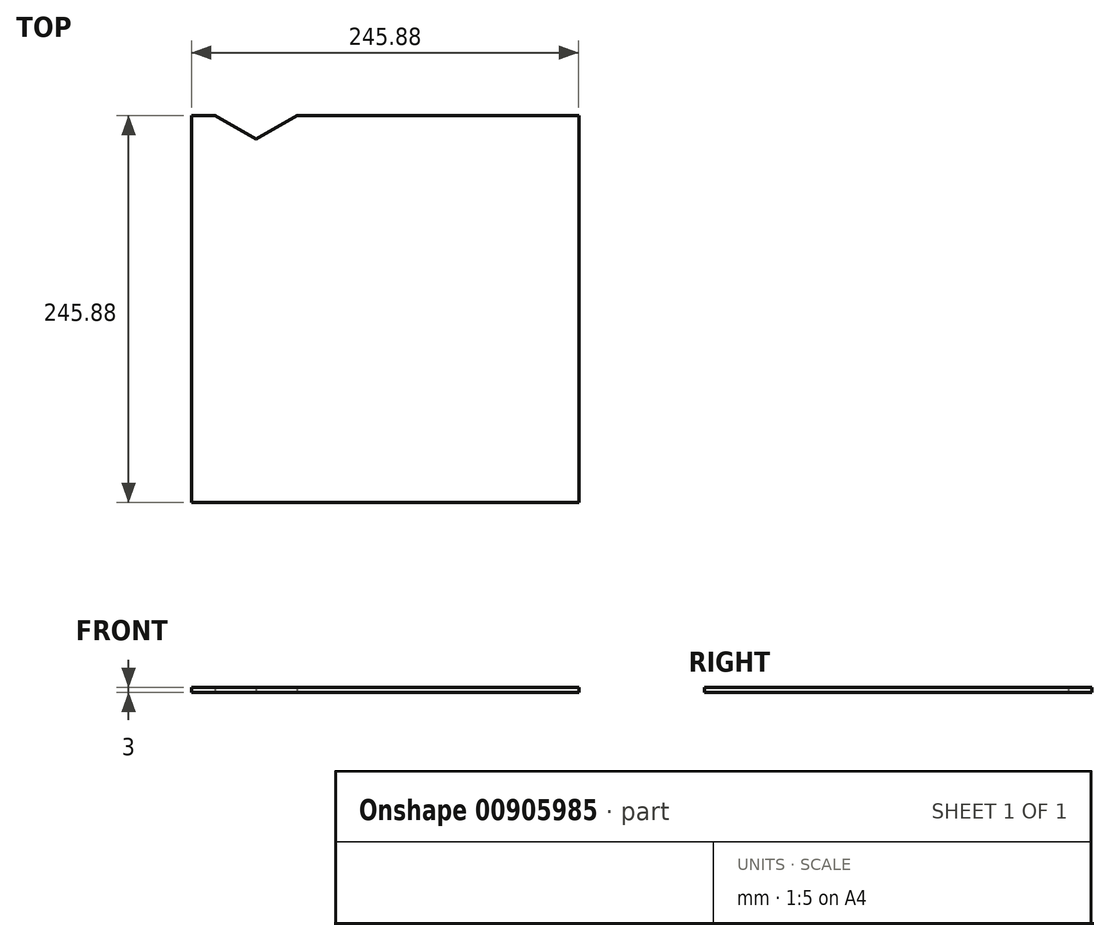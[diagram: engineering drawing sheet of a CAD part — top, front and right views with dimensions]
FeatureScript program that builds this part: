
annotation { "Feature Type Name" : "Feature", "Feature Type Description" : "" }
export const myFeature = defineFeature(function(context is Context, id is Id, definition is map)
    precondition{}
    {
        {
            var Q0;
            Q0=qCreatedBy(makeId("Top.planeOp"),FACE);
            var sketch = newSketch(context, id + "F0", { "sketchPlane" : qUnion([Q0])});
            skLineSegment(sketch, "E0", {"start": v(15, 0) * mm, "end": v(0, -25.98) * mm});
            skLineSegment(sketch, "E1", {"start": v(0, -25.98) * mm, "end": v(-15, 0) * mm});
            skLineSegment(sketch, "E2", {"start": v(-15, 0) * mm, "end": v(0, 25.98) * mm});
            skLineSegment(sketch, "E3", {"start": v(0, 25.98) * mm, "end": v(15, 0) * mm});
            skLineSegment(sketch, "E4", {"start": v(-15, 0) * mm, "end": v(-40.98, 15) * mm});
            skLineSegment(sketch, "E5", {"start": v(-40.98, 15) * mm, "end": v(-25.98, 40.98) * mm});
            skLineSegment(sketch, "E6", {"start": v(-25.98, 40.98) * mm, "end": v(0, 25.98) * mm});
            skLineSegment(sketch, "E7", {"start": v(0, 25.98) * mm, "end": v(25.98, 40.98) * mm});
            skLineSegment(sketch, "E8", {"start": v(25.98, 40.98) * mm, "end": v(40.98, 15) * mm});
            skLineSegment(sketch, "E9", {"start": v(40.98, 15) * mm, "end": v(15, 0) * mm});
            skLineSegment(sketch, "E10", {"start": v(15, 0) * mm, "end": v(40.98, -15) * mm});
            skLineSegment(sketch, "E11", {"start": v(40.98, -15) * mm, "end": v(25.98, -40.98) * mm});
            skLineSegment(sketch, "E12", {"start": v(25.98, -40.98) * mm, "end": v(0, -25.98) * mm});
            skLineSegment(sketch, "E13", {"start": v(-15, 0) * mm, "end": v(-40.98, -15) * mm});
            skLineSegment(sketch, "E14", {"start": v(-40.98, -15) * mm, "end": v(-25.98, -40.98) * mm});
            skLineSegment(sketch, "E15", {"start": v(-25.98, -40.98) * mm, "end": v(0, -25.98) * mm});
            skLineSegment(sketch, "E16", {"start": v(-40.98, 15) * mm, "end": v(-66.96, 0) * mm});
            skLineSegment(sketch, "E17", {"start": v(-66.96, 0) * mm, "end": v(-40.98, -15) * mm});
            skLineSegment(sketch, "E18", {"start": v(40.98, 15) * mm, "end": v(66.96, 0) * mm});
            skLineSegment(sketch, "E19", {"start": v(66.96, 0) * mm, "end": v(40.98, -15) * mm});
            skLineSegment(sketch, "E20", {"start": v(0, 25.98) * mm, "end": v(0, 55.98) * mm});
            skLineSegment(sketch, "E21", {"start": v(-25.98, 40.98) * mm, "end": v(0, 55.98) * mm});
            skLineSegment(sketch, "E22", {"start": v(25.98, 40.98) * mm, "end": v(0, 55.98) * mm});
            skLineSegment(sketch, "E23", {"start": v(0, -25.98) * mm, "end": v(0, -55.98) * mm});
            skLineSegment(sketch, "E24", {"start": v(0, -55.98) * mm, "end": v(-25.98, -40.98) * mm});
            skLineSegment(sketch, "E25", {"start": v(0, -55.98) * mm, "end": v(25.98, -40.98) * mm});
            skLineSegment(sketch, "E26", {"start": v(-40.98, 15) * mm, "end": v(-55.98, 40.98) * mm});
            skLineSegment(sketch, "E27", {"start": v(-55.98, 40.98) * mm, "end": v(-81.96, 25.98) * mm});
            skLineSegment(sketch, "E28", {"start": v(-81.96, 25.98) * mm, "end": v(-66.96, 0) * mm});
            skLineSegment(sketch, "E29", {"start": v(-40.98, -15) * mm, "end": v(-55.98, -40.98) * mm});
            skLineSegment(sketch, "E30", {"start": v(-55.98, -40.98) * mm, "end": v(-81.96, -25.98) * mm});
            skLineSegment(sketch, "E31", {"start": v(-81.96, -25.98) * mm, "end": v(-66.96, 0) * mm});
            skLineSegment(sketch, "E32", {"start": v(-55.98, 40.98) * mm, "end": v(-40.98, 66.96) * mm});
            skLineSegment(sketch, "E33", {"start": v(-40.98, 66.96) * mm, "end": v(-25.98, 40.98) * mm});
            skLineSegment(sketch, "E34", {"start": v(-40.98, 66.96) * mm, "end": v(-15, 81.96) * mm});
            skLineSegment(sketch, "E35", {"start": v(-15, 81.96) * mm, "end": v(0, 55.98) * mm});
            skLineSegment(sketch, "E36", {"start": v(-55.98, 40.98) * mm, "end": v(-81.96, 55.98) * mm});
            skLineSegment(sketch, "E37", {"start": v(-81.96, 55.98) * mm, "end": v(-66.96, 81.96) * mm});
            skLineSegment(sketch, "E38", {"start": v(-66.96, 81.96) * mm, "end": v(-40.98, 66.96) * mm});
            skLineSegment(sketch, "E39", {"start": v(15, 81.96) * mm, "end": v(40.98, 66.96) * mm});
            skLineSegment(sketch, "E40", {"start": v(40.98, 66.96) * mm, "end": v(25.98, 40.98) * mm});
            skLineSegment(sketch, "E41", {"start": v(40.98, 66.96) * mm, "end": v(55.98, 40.98) * mm});
            skLineSegment(sketch, "E42", {"start": v(55.98, 40.98) * mm, "end": v(40.98, 15) * mm});
            skLineSegment(sketch, "E43", {"start": v(-81.96, 55.98) * mm, "end": v(-81.96, 25.98) * mm});
            skLineSegment(sketch, "E44", {"start": v(-81.96, 25.98) * mm, "end": v(-107.94, 40.98) * mm});
            skLineSegment(sketch, "E45", {"start": v(-107.94, 40.98) * mm, "end": v(-81.96, 55.98) * mm});
            skLineSegment(sketch, "E46", {"start": v(55.98, 40.98) * mm, "end": v(81.96, 25.98) * mm});
            skLineSegment(sketch, "E47", {"start": v(81.96, 25.98) * mm, "end": v(66.96, 0) * mm});
            skLineSegment(sketch, "E48", {"start": v(55.98, 40.98) * mm, "end": v(81.96, 55.98) * mm});
            skLineSegment(sketch, "E49", {"start": v(81.96, 55.98) * mm, "end": v(66.96, 81.96) * mm});
            skLineSegment(sketch, "E50", {"start": v(66.96, 81.96) * mm, "end": v(40.98, 66.96) * mm});
            skLineSegment(sketch, "E51", {"start": v(81.96, 55.98) * mm, "end": v(81.96, 25.98) * mm});
            skLineSegment(sketch, "E52", {"start": v(81.96, 25.98) * mm, "end": v(107.94, 40.98) * mm});
            skLineSegment(sketch, "E53", {"start": v(107.94, 40.98) * mm, "end": v(81.96, 55.98) * mm});
            skLineSegment(sketch, "E54", {"start": v(81.96, 55.98) * mm, "end": v(96.96, 81.96) * mm});
            skLineSegment(sketch, "E55", {"start": v(96.96, 81.96) * mm, "end": v(122.94, 66.96) * mm});
            skLineSegment(sketch, "E56", {"start": v(122.94, 66.96) * mm, "end": v(107.94, 40.98) * mm});
            skLineSegment(sketch, "E57", {"start": v(-81.96, 55.98) * mm, "end": v(-96.96, 81.96) * mm});
            skLineSegment(sketch, "E58", {"start": v(-96.96, 81.96) * mm, "end": v(-122.94, 66.96) * mm});
            skLineSegment(sketch, "E59", {"start": v(-122.94, 66.96) * mm, "end": v(-107.94, 40.98) * mm});
            skLineSegment(sketch, "E60", {"start": v(-107.94, 40.98) * mm, "end": v(-122.94, 15) * mm});
            skLineSegment(sketch, "E61", {"start": v(-122.94, 15) * mm, "end": v(-96.96, 0) * mm});
            skLineSegment(sketch, "E62", {"start": v(-96.96, 0) * mm, "end": v(-81.96, 25.98) * mm});
            skLineSegment(sketch, "E63", {"start": v(-96.96, 0) * mm, "end": v(-81.96, -25.98) * mm});
            skLineSegment(sketch, "E64", {"start": v(-81.96, -25.98) * mm, "end": v(-107.94, -40.98) * mm});
            skLineSegment(sketch, "E65", {"start": v(-107.94, -40.98) * mm, "end": v(-122.94, -15) * mm});
            skLineSegment(sketch, "E66", {"start": v(-122.94, -15) * mm, "end": v(-96.96, 0) * mm});
            skLineSegment(sketch, "E67", {"start": v(81.96, 25.98) * mm, "end": v(96.96, 0) * mm});
            skLineSegment(sketch, "E68", {"start": v(96.96, 0) * mm, "end": v(122.94, 15) * mm});
            skLineSegment(sketch, "E69", {"start": v(122.94, 15) * mm, "end": v(107.94, 40.98) * mm});
            skLineSegment(sketch, "E70", {"start": v(66.96, 0) * mm, "end": v(81.96, -25.98) * mm});
            skLineSegment(sketch, "E71", {"start": v(81.96, -25.98) * mm, "end": v(96.96, 0) * mm});
            skLineSegment(sketch, "E72", {"start": v(81.96, -25.98) * mm, "end": v(107.94, -40.98) * mm});
            skLineSegment(sketch, "E73", {"start": v(107.94, -40.98) * mm, "end": v(122.94, -15) * mm});
            skLineSegment(sketch, "E74", {"start": v(122.94, -15) * mm, "end": v(96.96, 0) * mm});
            skLineSegment(sketch, "E75", {"start": v(40.98, 15) * mm, "end": v(40.98, -15) * mm});
            skLineSegment(sketch, "E76", {"start": v(81.96, -25.98) * mm, "end": v(55.98, -40.98) * mm});
            skLineSegment(sketch, "E77", {"start": v(55.98, -40.98) * mm, "end": v(40.98, -15) * mm});
            skLineSegment(sketch, "E78", {"start": v(-40.98, 15) * mm, "end": v(-40.98, -15) * mm});
            skLineSegment(sketch, "E79", {"start": v(-81.96, -25.98) * mm, "end": v(-81.96, -55.98) * mm});
            skLineSegment(sketch, "E80", {"start": v(-81.96, -55.98) * mm, "end": v(-107.94, -40.98) * mm});
            skLineSegment(sketch, "E81", {"start": v(-81.96, -55.98) * mm, "end": v(-55.98, -40.98) * mm});
            skLineSegment(sketch, "E82", {"start": v(-55.98, -40.98) * mm, "end": v(-40.98, -66.96) * mm});
            skLineSegment(sketch, "E83", {"start": v(-40.98, -66.96) * mm, "end": v(-25.98, -40.98) * mm});
            skLineSegment(sketch, "E84", {"start": v(-81.96, -55.98) * mm, "end": v(-66.96, -81.96) * mm});
            skLineSegment(sketch, "E85", {"start": v(-66.96, -81.96) * mm, "end": v(-40.98, -66.96) * mm});
            skLineSegment(sketch, "E86", {"start": v(-107.94, -40.98) * mm, "end": v(-122.94, -66.96) * mm});
            skLineSegment(sketch, "E87", {"start": v(-81.96, -55.98) * mm, "end": v(-96.96, -81.96) * mm});
            skLineSegment(sketch, "E88", {"start": v(-122.94, -66.96) * mm, "end": v(-96.96, -81.96) * mm});
            skLineSegment(sketch, "E89", {"start": v(-40.98, -66.96) * mm, "end": v(-15, -81.96) * mm});
            skLineSegment(sketch, "E90", {"start": v(-15, -81.96) * mm, "end": v(0, -55.98) * mm});
            skLineSegment(sketch, "E91", {"start": v(25.98, -40.98) * mm, "end": v(40.98, -66.96) * mm});
            skLineSegment(sketch, "E92", {"start": v(40.98, -66.96) * mm, "end": v(55.98, -40.98) * mm});
            skLineSegment(sketch, "E93", {"start": v(40.98, -66.96) * mm, "end": v(15, -81.96) * mm});
            skLineSegment(sketch, "E94", {"start": v(15, -81.96) * mm, "end": v(0, -55.98) * mm});
            skLineSegment(sketch, "E95", {"start": v(55.98, -40.98) * mm, "end": v(81.96, -55.98) * mm});
            skLineSegment(sketch, "E96", {"start": v(81.96, -55.98) * mm, "end": v(66.96, -81.96) * mm});
            skLineSegment(sketch, "E97", {"start": v(81.96, -55.98) * mm, "end": v(107.94, -40.98) * mm});
            skLineSegment(sketch, "E98", {"start": v(82.15, -26.2) * mm, "end": v(81.96, -55.98) * mm});
            skLineSegment(sketch, "E99", {"start": v(40.98, -66.96) * mm, "end": v(66.96, -81.96) * mm});
            skLineSegment(sketch, "E100", {"start": v(96.96, -81.96) * mm, "end": v(122.94, -66.96) * mm});
            skLineSegment(sketch, "E101", {"start": v(122.94, -66.96) * mm, "end": v(107.94, -40.98) * mm});
            skLineSegment(sketch, "E102", {"start": v(-96.96, -81.96) * mm, "end": v(-81.96, -107.94) * mm});
            skLineSegment(sketch, "E103", {"start": v(-81.96, -107.94) * mm, "end": v(-66.96, -81.96) * mm});
            skLineSegment(sketch, "E104", {"start": v(-15, -81.96) * mm, "end": v(0, -107.94) * mm});
            skLineSegment(sketch, "E105", {"start": v(0, -107.94) * mm, "end": v(15, -81.96) * mm});
            skLineSegment(sketch, "E106", {"start": v(66.96, -81.96) * mm, "end": v(81.96, -107.94) * mm});
            skLineSegment(sketch, "E107", {"start": v(81.96, -107.94) * mm, "end": v(96.96, -81.96) * mm});
            skLineSegment(sketch, "E108", {"start": v(40.98, -66.96) * mm, "end": v(40.98, -96.96) * mm});
            skLineSegment(sketch, "E109", {"start": v(40.98, -96.96) * mm, "end": v(15, -81.96) * mm});
            skLineSegment(sketch, "E110", {"start": v(40.98, -96.96) * mm, "end": v(66.96, -81.96) * mm});
            skLineSegment(sketch, "E111", {"start": v(-66.96, -81.96) * mm, "end": v(-40.98, -96.96) * mm});
            skLineSegment(sketch, "E112", {"start": v(-40.98, -96.96) * mm, "end": v(-15, -81.96) * mm});
            skLineSegment(sketch, "E113", {"start": v(-40.98, -66.96) * mm, "end": v(-40.98, -96.96) * mm});
            skLineSegment(sketch, "E114", {"start": v(-96.96, -81.96) * mm, "end": v(-122.94, -96.96) * mm});
            skLineSegment(sketch, "E115", {"start": v(-122.94, -96.96) * mm, "end": v(-122.94, -66.96) * mm});
            skLineSegment(sketch, "E116", {"start": v(122.94, 15) * mm, "end": v(122.94, -15) * mm});
            skLineSegment(sketch, "E117", {"start": v(-81.96, -107.94) * mm, "end": v(-55.98, -122.94) * mm});
            skLineSegment(sketch, "E118", {"start": v(-40.98, -96.96) * mm, "end": v(-55.98, -122.94) * mm});
            skLineSegment(sketch, "E119", {"start": v(-40.98, -96.96) * mm, "end": v(-25.98, -122.94) * mm});
            skLineSegment(sketch, "E120", {"start": v(-25.98, -122.94) * mm, "end": v(0, -107.94) * mm});
            skLineSegment(sketch, "E121", {"start": v(0, -107.94) * mm, "end": v(25.98, -122.94) * mm});
            skLineSegment(sketch, "E122", {"start": v(25.98, -122.94) * mm, "end": v(40.98, -96.96) * mm});
            skLineSegment(sketch, "E123", {"start": v(40.98, -96.96) * mm, "end": v(55.98, -122.94) * mm});
            skLineSegment(sketch, "E124", {"start": v(55.98, -122.94) * mm, "end": v(81.96, -107.94) * mm});
            skLineSegment(sketch, "E125", {"start": v(-81.96, -107.94) * mm, "end": v(-107.94, -122.94) * mm});
            skLineSegment(sketch, "E126", {"start": v(-107.94, -122.94) * mm, "end": v(-122.94, -96.96) * mm});
            skLineSegment(sketch, "E127", {"start": v(81.96, -107.94) * mm, "end": v(107.94, -122.94) * mm});
            skLineSegment(sketch, "E128", {"start": v(107.94, -122.94) * mm, "end": v(122.94, -96.96) * mm});
            skLineSegment(sketch, "E129", {"start": v(122.94, -96.96) * mm, "end": v(96.96, -81.96) * mm});
            skLineSegment(sketch, "E130", {"start": v(122.94, -66.96) * mm, "end": v(122.94, -96.96) * mm});
            skLineSegment(sketch, "E131", {"start": v(25.98, -122.94) * mm, "end": v(55.98, -122.94) * mm});
            skLineSegment(sketch, "E132", {"start": v(-25.98, -122.94) * mm, "end": v(25.98, -122.94) * mm});
            skLineSegment(sketch, "E133", {"start": v(-107.94, -122.94) * mm, "end": v(-55.98, -122.94) * mm});
            skLineSegment(sketch, "E134", {"start": v(-25.98, -122.94) * mm, "end": v(-55.98, -122.94) * mm});
            skLineSegment(sketch, "E135", {"start": v(55.98, -122.94) * mm, "end": v(107.94, -122.94) * mm});
            skLineSegment(sketch, "E136", {"start": v(107.94, -122.94) * mm, "end": v(122.94, -122.94) * mm});
            skLineSegment(sketch, "E137", {"start": v(122.94, -122.94) * mm, "end": v(122.94, -96.96) * mm});
            skLineSegment(sketch, "E138", {"start": v(122.94, -15) * mm, "end": v(122.94, -66.96) * mm});
            skLineSegment(sketch, "E139", {"start": v(122.94, 15) * mm, "end": v(122.94, 66.96) * mm});
            skLineSegment(sketch, "E140", {"start": v(-107.94, -122.94) * mm, "end": v(-122.94, -122.94) * mm});
            skLineSegment(sketch, "E141", {"start": v(-122.94, -122.94) * mm, "end": v(-122.94, -96.96) * mm});
            skLineSegment(sketch, "E142", {"start": v(81.96, -55.98) * mm, "end": v(96.96, -81.96) * mm});
            skLineSegment(sketch, "E143", {"start": v(-122.94, -15) * mm, "end": v(-122.94, -66.96) * mm});
            skLineSegment(sketch, "E144", {"start": v(-122.94, 15) * mm, "end": v(-122.94, -15) * mm});
            skLineSegment(sketch, "E145", {"start": v(-122.94, 15) * mm, "end": v(-122.94, 66.96) * mm});
            skLineSegment(sketch, "E146", {"start": v(15, 81.96) * mm, "end": v(0, 55.98) * mm});
            skLineSegment(sketch, "E147", {"start": v(-15, 81.96) * mm, "end": v(0, 107.94) * mm});
            skLineSegment(sketch, "E148", {"start": v(0, 107.94) * mm, "end": v(15, 81.96) * mm});
            skLineSegment(sketch, "E149", {"start": v(15, 81.96) * mm, "end": v(40.98, 96.96) * mm});
            skLineSegment(sketch, "E150", {"start": v(40.98, 96.96) * mm, "end": v(66.96, 81.96) * mm});
            skLineSegment(sketch, "E151", {"start": v(40.98, 96.96) * mm, "end": v(40.98, 66.96) * mm});
            skLineSegment(sketch, "E152", {"start": v(66.96, 81.96) * mm, "end": v(81.96, 107.94) * mm});
            skLineSegment(sketch, "E153", {"start": v(81.96, 107.94) * mm, "end": v(96.96, 81.96) * mm});
            skLineSegment(sketch, "E154", {"start": v(96.96, 81.96) * mm, "end": v(122.94, 96.96) * mm});
            skLineSegment(sketch, "E155", {"start": v(122.94, 96.96) * mm, "end": v(122.94, 66.96) * mm});
            skLineSegment(sketch, "E156", {"start": v(81.96, 107.94) * mm, "end": v(107.94, 122.94) * mm});
            skLineSegment(sketch, "E157", {"start": v(107.94, 122.94) * mm, "end": v(122.94, 96.96) * mm});
            skLineSegment(sketch, "E158", {"start": v(81.96, 107.94) * mm, "end": v(55.98, 122.94) * mm});
            skLineSegment(sketch, "E159", {"start": v(55.98, 122.94) * mm, "end": v(40.98, 96.96) * mm});
            skLineSegment(sketch, "E160", {"start": v(40.98, 96.96) * mm, "end": v(25.98, 122.94) * mm});
            skLineSegment(sketch, "E161", {"start": v(25.98, 122.94) * mm, "end": v(0, 107.94) * mm});
            skLineSegment(sketch, "E162", {"start": v(-15, 81.96) * mm, "end": v(-40.98, 96.96) * mm});
            skLineSegment(sketch, "E163", {"start": v(-40.98, 96.96) * mm, "end": v(-40.98, 66.96) * mm});
            skLineSegment(sketch, "E164", {"start": v(-66.96, 81.96) * mm, "end": v(-40.98, 96.96) * mm});
            skLineSegment(sketch, "E165", {"start": v(-66.96, 81.96) * mm, "end": v(-81.96, 107.94) * mm});
            skLineSegment(sketch, "E166", {"start": v(-81.96, 107.94) * mm, "end": v(-96.96, 81.96) * mm});
            skLineSegment(sketch, "E167", {"start": v(-96.96, 81.96) * mm, "end": v(-122.94, 96.96) * mm});
            skLineSegment(sketch, "E168", {"start": v(-122.94, 96.96) * mm, "end": v(-122.94, 66.96) * mm});
            skLineSegment(sketch, "E169", {"start": v(-122.94, 96.96) * mm, "end": v(-107.94, 122.94) * mm});
            skLineSegment(sketch, "E170", {"start": v(-107.94, 122.94) * mm, "end": v(-81.96, 107.94) * mm});
            skLineSegment(sketch, "E171", {"start": v(-55.98, 122.94) * mm, "end": v(-40.98, 96.96) * mm});
            skLineSegment(sketch, "E172", {"start": v(-40.98, 96.96) * mm, "end": v(-25.98, 122.94) * mm});
            skLineSegment(sketch, "E173", {"start": v(-25.98, 122.94) * mm, "end": v(0, 107.94) * mm});
            skLineSegment(sketch, "E174", {"start": v(-55.98, 122.94) * mm, "end": v(-25.98, 122.94) * mm});
            skLineSegment(sketch, "E175", {"start": v(-55.98, 122.94) * mm, "end": v(-107.94, 122.94) * mm});
            skLineSegment(sketch, "E176", {"start": v(-107.94, 122.94) * mm, "end": v(-122.94, 122.94) * mm});
            skLineSegment(sketch, "E177", {"start": v(-122.94, 122.94) * mm, "end": v(-122.94, 96.96) * mm});
            skLineSegment(sketch, "E178", {"start": v(-25.98, 122.94) * mm, "end": v(25.98, 122.94) * mm});
            skLineSegment(sketch, "E179", {"start": v(55.98, 122.94) * mm, "end": v(25.98, 122.94) * mm});
            skLineSegment(sketch, "E180", {"start": v(55.98, 122.94) * mm, "end": v(107.94, 122.94) * mm});
            skLineSegment(sketch, "E181", {"start": v(107.94, 122.94) * mm, "end": v(122.94, 122.94) * mm});
            skLineSegment(sketch, "E182", {"start": v(122.94, 122.94) * mm, "end": v(122.94, 96.96) * mm});
            skLineSegment(sketch, "E183", {"start": v(-81.96, 107.94) * mm, "end": v(-55.98, 122.94) * mm});
            skSolve(sketch);
        }
        {
            var Q0;
            Q0=makeQuery(id+"F0.imprint","IMPRINT",FACE,{"disambiguationData":[TD([[makeQuery(id+"F0.imprint","IMPRINT",EDGE,{"derivedFrom":sQuery(id+"F0.wireOp",EDGE,"E164")}),1.0]])]});
            var Q1;
            Q1=makeQuery(id+"F0.imprint","IMPRINT",FACE,{"disambiguationData":[TD([[makeQuery(id+"F0.imprint","IMPRINT",EDGE,{"derivedFrom":sQuery(id+"F0.wireOp",EDGE,"E169")}),1.0]])]});
            var Q2;
            Q2=makeQuery(id+"F0.imprint","IMPRINT",FACE,{"disambiguationData":[TD([[makeQuery(id+"F0.imprint","IMPRINT",EDGE,{"derivedFrom":sQuery(id+"F0.wireOp",EDGE,"E58")}),-1.0]])]});
            var Q3;
            Q3=makeQuery(id+"F0.imprint","IMPRINT",FACE,{"disambiguationData":[TD([[makeQuery(id+"F0.imprint","IMPRINT",EDGE,{"derivedFrom":sQuery(id+"F0.wireOp",EDGE,"E37")}),1.0]])]});
            var Q4;
            Q4=makeQuery(id+"F0.imprint","IMPRINT",FACE,{"disambiguationData":[TD([[makeQuery(id+"F0.imprint","IMPRINT",EDGE,{"derivedFrom":sQuery(id+"F0.wireOp",EDGE,"E50")}),-1.0]])]});
            var Q5;
            Q5=makeQuery(id+"F0.imprint","IMPRINT",FACE,{"disambiguationData":[TD([[makeQuery(id+"F0.imprint","IMPRINT",EDGE,{"derivedFrom":sQuery(id+"F0.wireOp",EDGE,"E126")}),1.0]])]});
            var Q6;
            Q6=makeQuery(id+"F0.imprint","IMPRINT",FACE,{"disambiguationData":[TD([[makeQuery(id+"F0.imprint","IMPRINT",EDGE,{"derivedFrom":sQuery(id+"F0.wireOp",EDGE,"E117")}),-1.0]])]});
            var Q7;
            Q7=makeQuery(id+"F0.imprint","IMPRINT",FACE,{"disambiguationData":[TD([[makeQuery(id+"F0.imprint","IMPRINT",EDGE,{"derivedFrom":sQuery(id+"F0.wireOp",EDGE,"E84")}),-1.0]])]});
            var Q8;
            Q8=makeQuery(id+"F0.imprint","IMPRINT",FACE,{"disambiguationData":[TD([[makeQuery(id+"F0.imprint","IMPRINT",EDGE,{"derivedFrom":sQuery(id+"F0.wireOp",EDGE,"E80")}),1.0]])]});
            var Q9;
            Q9=makeQuery(id+"F0.imprint","IMPRINT",FACE,{"disambiguationData":[TD([[makeQuery(id+"F0.imprint","IMPRINT",EDGE,{"derivedFrom":sQuery(id+"F0.wireOp",EDGE,"E85")}),-1.0]])]});
            var Q10;
            Q10=makeQuery(id+"F0.imprint","IMPRINT",FACE,{"disambiguationData":[TD([[makeQuery(id+"F0.imprint","IMPRINT",EDGE,{"derivedFrom":sQuery(id+"F0.wireOp",EDGE,"E81")}),-1.0]])]});
            var Q11;
            Q11=makeQuery(id+"F0.imprint","IMPRINT",FACE,{"disambiguationData":[TD([[makeQuery(id+"F0.imprint","IMPRINT",EDGE,{"derivedFrom":sQuery(id+"F0.wireOp",EDGE,"E4")}),1.0]])]});
            var Q12;
            Q12=makeQuery(id+"F0.imprint","IMPRINT",FACE,{"disambiguationData":[TD([[makeQuery(id+"F0.imprint","IMPRINT",EDGE,{"derivedFrom":sQuery(id+"F0.wireOp",EDGE,"E44")}),1.0]])]});
            var Q13;
            Q13=makeQuery(id+"F0.imprint","IMPRINT",FACE,{"disambiguationData":[TD([[makeQuery(id+"F0.imprint","IMPRINT",EDGE,{"derivedFrom":sQuery(id+"F0.wireOp",EDGE,"E28")}),-1.0]])]});
            var Q14;
            Q14=makeQuery(id+"F0.imprint","IMPRINT",FACE,{"disambiguationData":[TD([[makeQuery(id+"F0.imprint","IMPRINT",EDGE,{"derivedFrom":sQuery(id+"F0.wireOp",EDGE,"E61")}),-1.0]])]});
            var Q15;
            Q15=makeQuery(id+"F0.imprint","IMPRINT",FACE,{"disambiguationData":[TD([[makeQuery(id+"F0.imprint","IMPRINT",EDGE,{"derivedFrom":sQuery(id+"F0.wireOp",EDGE,"E45")}),1.0]])]});
            var Q16;
            Q16=makeQuery(id+"F0.imprint","IMPRINT",FACE,{"disambiguationData":[TD([[makeQuery(id+"F0.imprint","IMPRINT",EDGE,{"derivedFrom":sQuery(id+"F0.wireOp",EDGE,"E59")}),-1.0]])]});
            var Q17;
            Q17=makeQuery(id+"F0.imprint","IMPRINT",FACE,{"disambiguationData":[TD([[makeQuery(id+"F0.imprint","IMPRINT",EDGE,{"derivedFrom":sQuery(id+"F0.wireOp",EDGE,"E166")}),-1.0]])]});
            var Q18;
            Q18=makeQuery(id+"F0.imprint","IMPRINT",FACE,{"disambiguationData":[TD([[makeQuery(id+"F0.imprint","IMPRINT",EDGE,{"derivedFrom":sQuery(id+"F0.wireOp",EDGE,"E27")}),-1.0]])]});
            var Q19;
            Q19=makeQuery(id+"F0.imprint","IMPRINT",FACE,{"disambiguationData":[TD([[makeQuery(id+"F0.imprint","IMPRINT",EDGE,{"derivedFrom":sQuery(id+"F0.wireOp",EDGE,"E41")}),1.0]])]});
            var Q20;
            Q20=makeQuery(id+"F0.imprint","IMPRINT",FACE,{"disambiguationData":[TD([[makeQuery(id+"F0.imprint","IMPRINT",EDGE,{"derivedFrom":sQuery(id+"F0.wireOp",EDGE,"E22")}),-1.0]])]});
            var Q21;
            Q21=makeQuery(id+"F0.imprint","IMPRINT",FACE,{"disambiguationData":[TD([[makeQuery(id+"F0.imprint","IMPRINT",EDGE,{"derivedFrom":sQuery(id+"F0.wireOp",EDGE,"E49")}),-1.0]])]});
            var Q22;
            Q22=makeQuery(id+"F0.imprint","IMPRINT",FACE,{"disambiguationData":[TD([[makeQuery(id+"F0.imprint","IMPRINT",EDGE,{"derivedFrom":sQuery(id+"F0.wireOp",EDGE,"E39")}),1.0]])]});
            var Q23;
            Q23=makeQuery(id+"F0.imprint","IMPRINT",FACE,{"disambiguationData":[TD([[makeQuery(id+"F0.imprint","IMPRINT",EDGE,{"derivedFrom":sQuery(id+"F0.wireOp",EDGE,"E89")}),-1.0]])]});
            var Q24;
            Q24=makeQuery(id+"F0.imprint","IMPRINT",FACE,{"disambiguationData":[TD([[makeQuery(id+"F0.imprint","IMPRINT",EDGE,{"derivedFrom":sQuery(id+"F0.wireOp",EDGE,"E103")}),-1.0]])]});
            var Q25;
            Q25=makeQuery(id+"F0.imprint","IMPRINT",FACE,{"disambiguationData":[TD([[makeQuery(id+"F0.imprint","IMPRINT",EDGE,{"derivedFrom":sQuery(id+"F0.wireOp",EDGE,"E24")}),1.0]])]});
            var Q26;
            Q26=makeQuery(id+"F0.imprint","IMPRINT",FACE,{"disambiguationData":[TD([[makeQuery(id+"F0.imprint","IMPRINT",EDGE,{"derivedFrom":sQuery(id+"F0.wireOp",EDGE,"E14")}),-1.0]])]});
            var Q27;
            Q27=makeQuery(id+"F0.imprint","IMPRINT",FACE,{"disambiguationData":[TD([[makeQuery(id+"F0.imprint","IMPRINT",EDGE,{"derivedFrom":sQuery(id+"F0.wireOp",EDGE,"E30")}),1.0]])]});
            var Q28;
            Q28=makeQuery(id+"F0.imprint","IMPRINT",FACE,{"disambiguationData":[TD([[makeQuery(id+"F0.imprint","IMPRINT",EDGE,{"derivedFrom":sQuery(id+"F0.wireOp",EDGE,"E102")}),-1.0]])]});
            var Q29;
            Q29=makeQuery(id+"F0.imprint","IMPRINT",FACE,{"disambiguationData":[TD([[makeQuery(id+"F0.imprint","IMPRINT",EDGE,{"derivedFrom":sQuery(id+"F0.wireOp",EDGE,"E88")}),-1.0]])]});
            var Q30;
            Q30=makeQuery(id+"F0.imprint","IMPRINT",FACE,{"disambiguationData":[TD([[makeQuery(id+"F0.imprint","IMPRINT",EDGE,{"derivedFrom":sQuery(id+"F0.wireOp",EDGE,"E120")}),-1.0]])]});
            var Q31;
            Q31=makeQuery(id+"F0.imprint","IMPRINT",FACE,{"disambiguationData":[TD([[makeQuery(id+"F0.imprint","IMPRINT",EDGE,{"derivedFrom":sQuery(id+"F0.wireOp",EDGE,"E105")}),-1.0]])]});
            var Q32;
            Q32=makeQuery(id+"F0.imprint","IMPRINT",FACE,{"disambiguationData":[TD([[makeQuery(id+"F0.imprint","IMPRINT",EDGE,{"derivedFrom":sQuery(id+"F0.wireOp",EDGE,"E104")}),-1.0]])]});
            var Q33;
            Q33=makeQuery(id+"F0.imprint","IMPRINT",FACE,{"disambiguationData":[TD([[makeQuery(id+"F0.imprint","IMPRINT",EDGE,{"derivedFrom":sQuery(id+"F0.wireOp",EDGE,"E118")}),1.0]])]});
            var Q34;
            Q34=makeQuery(id+"F0.imprint","IMPRINT",FACE,{"disambiguationData":[TD([[makeQuery(id+"F0.imprint","IMPRINT",EDGE,{"derivedFrom":sQuery(id+"F0.wireOp",EDGE,"E171")}),1.0]])]});
            var Q35;
            Q35=makeQuery(id+"F0.imprint","IMPRINT",FACE,{"disambiguationData":[TD([[makeQuery(id+"F0.imprint","IMPRINT",EDGE,{"derivedFrom":sQuery(id+"F0.wireOp",EDGE,"E161")}),-1.0]])]});
            var Q36;
            Q36=makeQuery(id+"F0.imprint","IMPRINT",FACE,{"disambiguationData":[TD([[makeQuery(id+"F0.imprint","IMPRINT",EDGE,{"derivedFrom":sQuery(id+"F0.wireOp",EDGE,"E148")}),1.0]])]});
            var Q37;
            Q37=makeQuery(id+"F0.imprint","IMPRINT",FACE,{"disambiguationData":[TD([[makeQuery(id+"F0.imprint","IMPRINT",EDGE,{"derivedFrom":sQuery(id+"F0.wireOp",EDGE,"E147")}),1.0]])]});
            var Q38;
            Q38=makeQuery(id+"F0.imprint","IMPRINT",FACE,{"disambiguationData":[TD([[makeQuery(id+"F0.imprint","IMPRINT",EDGE,{"derivedFrom":sQuery(id+"F0.wireOp",EDGE,"E150")}),1.0]])]});
            var Q39;
            Q39=makeQuery(id+"F0.imprint","IMPRINT",FACE,{"disambiguationData":[TD([[makeQuery(id+"F0.imprint","IMPRINT",EDGE,{"derivedFrom":sQuery(id+"F0.wireOp",EDGE,"E159")}),-1.0]])]});
            var Q40;
            Q40=makeQuery(id+"F0.imprint","IMPRINT",FACE,{"disambiguationData":[TD([[makeQuery(id+"F0.imprint","IMPRINT",EDGE,{"derivedFrom":sQuery(id+"F0.wireOp",EDGE,"E156")}),1.0]])]});
            var Q41;
            Q41=makeQuery(id+"F0.imprint","IMPRINT",FACE,{"disambiguationData":[TD([[makeQuery(id+"F0.imprint","IMPRINT",EDGE,{"derivedFrom":sQuery(id+"F0.wireOp",EDGE,"E157")}),1.0]])]});
            var Q42;
            Q42=makeQuery(id+"F0.imprint","IMPRINT",FACE,{"disambiguationData":[TD([[makeQuery(id+"F0.imprint","IMPRINT",EDGE,{"derivedFrom":sQuery(id+"F0.wireOp",EDGE,"E15")}),-1.0]])]});
            var Q43;
            Q43=makeQuery(id+"F0.imprint","IMPRINT",FACE,{"disambiguationData":[TD([[makeQuery(id+"F0.imprint","IMPRINT",EDGE,{"derivedFrom":sQuery(id+"F0.wireOp",EDGE,"E153")}),1.0]])]});
            var Q44;
            Q44=makeQuery(id+"F0.imprint","IMPRINT",FACE,{"disambiguationData":[TD([[makeQuery(id+"F0.imprint","IMPRINT",EDGE,{"derivedFrom":sQuery(id+"F0.wireOp",EDGE,"E43")}),-1.0]])]});
            var Q45;
            Q45=makeQuery(id+"F0.imprint","IMPRINT",FACE,{"disambiguationData":[TD([[makeQuery(id+"F0.imprint","IMPRINT",EDGE,{"derivedFrom":sQuery(id+"F0.wireOp",EDGE,"E65")}),1.0]])]});
            var Q46;
            Q46=makeQuery(id+"F0.imprint","IMPRINT",FACE,{"disambiguationData":[TD([[makeQuery(id+"F0.imprint","IMPRINT",EDGE,{"derivedFrom":sQuery(id+"F0.wireOp",EDGE,"E38")}),1.0]])]});
            var Q47;
            Q47=makeQuery(id+"F0.imprint","IMPRINT",FACE,{"disambiguationData":[TD([[makeQuery(id+"F0.imprint","IMPRINT",EDGE,{"derivedFrom":sQuery(id+"F0.wireOp",EDGE,"E64")}),1.0]])]});
            var Q48;
            Q48=makeQuery(id+"F0.imprint","IMPRINT",FACE,{"disambiguationData":[TD([[makeQuery(id+"F0.imprint","IMPRINT",EDGE,{"derivedFrom":sQuery(id+"F0.wireOp",EDGE,"E63")}),-1.0]])]});
            var Q49;
            Q49=makeQuery(id+"F0.imprint","IMPRINT",FACE,{"disambiguationData":[TD([[makeQuery(id+"F0.imprint","IMPRINT",EDGE,{"derivedFrom":sQuery(id+"F0.wireOp",EDGE,"E100")}),-1.0]])]});
            var Q50;
            Q50=makeQuery(id+"F0.imprint","IMPRINT",FACE,{"disambiguationData":[TD([[makeQuery(id+"F0.imprint","IMPRINT",EDGE,{"derivedFrom":sQuery(id+"F0.wireOp",EDGE,"E107")}),-1.0]])]});
            var Q51;
            Q51=makeQuery(id+"F0.imprint","IMPRINT",FACE,{"disambiguationData":[TD([[makeQuery(id+"F0.imprint","IMPRINT",EDGE,{"derivedFrom":sQuery(id+"F0.wireOp",EDGE,"E99")}),-1.0]])]});
            var Q52;
            Q52=makeQuery(id+"F0.imprint","IMPRINT",FACE,{"disambiguationData":[TD([[makeQuery(id+"F0.imprint","IMPRINT",EDGE,{"derivedFrom":sQuery(id+"F0.wireOp",EDGE,"E92")}),-1.0]])]});
            var Q53;
            Q53=makeQuery(id+"F0.imprint","IMPRINT",FACE,{"disambiguationData":[TD([[makeQuery(id+"F0.imprint","IMPRINT",EDGE,{"derivedFrom":sQuery(id+"F0.wireOp",EDGE,"E34")}),1.0]])]});
            var Q54;
            Q54=makeQuery(id+"F0.imprint","IMPRINT",FACE,{"disambiguationData":[TD([[makeQuery(id+"F0.imprint","IMPRINT",EDGE,{"derivedFrom":sQuery(id+"F0.wireOp",EDGE,"E93")}),1.0]])]});
            var Q55;
            Q55=makeQuery(id+"F0.imprint","IMPRINT",FACE,{"disambiguationData":[TD([[makeQuery(id+"F0.imprint","IMPRINT",EDGE,{"derivedFrom":sQuery(id+"F0.wireOp",EDGE,"E124")}),-1.0]])]});
            var Q56;
            Q56=makeQuery(id+"F0.imprint","IMPRINT",FACE,{"disambiguationData":[TD([[makeQuery(id+"F0.imprint","IMPRINT",EDGE,{"derivedFrom":sQuery(id+"F0.wireOp",EDGE,"E35")}),1.0]])]});
            var Q57;
            Q57=makeQuery(id+"F0.imprint","IMPRINT",FACE,{"disambiguationData":[TD([[makeQuery(id+"F0.imprint","IMPRINT",EDGE,{"derivedFrom":sQuery(id+"F0.wireOp",EDGE,"E122")}),-1.0]])]});
            var Q58;
            Q58=makeQuery(id+"F0.imprint","IMPRINT",FACE,{"disambiguationData":[TD([[makeQuery(id+"F0.imprint","IMPRINT",EDGE,{"derivedFrom":sQuery(id+"F0.wireOp",EDGE,"E0")}),-1.0]])]});
            var Q59;
            Q59=makeQuery(id+"F0.imprint","IMPRINT",FACE,{"disambiguationData":[TD([[makeQuery(id+"F0.imprint","IMPRINT",EDGE,{"derivedFrom":sQuery(id+"F0.wireOp",EDGE,"E3")}),1.0]])]});
            var Q60;
            Q60=makeQuery(id+"F0.imprint","IMPRINT",FACE,{"disambiguationData":[TD([[makeQuery(id+"F0.imprint","IMPRINT",EDGE,{"derivedFrom":sQuery(id+"F0.wireOp",EDGE,"E55")}),1.0]])]});
            var Q61;
            Q61=makeQuery(id+"F0.imprint","IMPRINT",FACE,{"disambiguationData":[TD([[makeQuery(id+"F0.imprint","IMPRINT",EDGE,{"derivedFrom":sQuery(id+"F0.wireOp",EDGE,"E8")}),1.0]])]});
            var Q62;
            Q62=makeQuery(id+"F0.imprint","IMPRINT",FACE,{"disambiguationData":[TD([[makeQuery(id+"F0.imprint","IMPRINT",EDGE,{"derivedFrom":sQuery(id+"F0.wireOp",EDGE,"E12")}),1.0]])]});
            var Q63;
            Q63=makeQuery(id+"F0.imprint","IMPRINT",FACE,{"disambiguationData":[TD([[makeQuery(id+"F0.imprint","IMPRINT",EDGE,{"derivedFrom":sQuery(id+"F0.wireOp",EDGE,"E71")}),-1.0]])]});
            var Q64;
            Q64=makeQuery(id+"F0.imprint","IMPRINT",FACE,{"disambiguationData":[TD([[makeQuery(id+"F0.imprint","IMPRINT",EDGE,{"derivedFrom":sQuery(id+"F0.wireOp",EDGE,"E18")}),-1.0]])]});
            var Q65;
            Q65=makeQuery(id+"F0.imprint","IMPRINT",FACE,{"disambiguationData":[TD([[makeQuery(id+"F0.imprint","IMPRINT",EDGE,{"derivedFrom":sQuery(id+"F0.wireOp",EDGE,"E56")}),1.0]])]});
            var Q66;
            Q66=makeQuery(id+"F0.imprint","IMPRINT",FACE,{"disambiguationData":[TD([[makeQuery(id+"F0.imprint","IMPRINT",EDGE,{"derivedFrom":sQuery(id+"F0.wireOp",EDGE,"E11")}),1.0]])]});
            var Q67;
            Q67=makeQuery(id+"F0.imprint","IMPRINT",FACE,{"disambiguationData":[TD([[makeQuery(id+"F0.imprint","IMPRINT",EDGE,{"derivedFrom":sQuery(id+"F0.wireOp",EDGE,"E47")}),1.0]])]});
            var Q68;
            Q68=makeQuery(id+"F0.imprint","IMPRINT",FACE,{"disambiguationData":[TD([[makeQuery(id+"F0.imprint","IMPRINT",EDGE,{"derivedFrom":sQuery(id+"F0.wireOp",EDGE,"E0")}),1.0]])]});
            var Q69;
            Q69=makeQuery(id+"F0.imprint","IMPRINT",FACE,{"disambiguationData":[TD([[makeQuery(id+"F0.imprint","IMPRINT",EDGE,{"derivedFrom":sQuery(id+"F0.wireOp",EDGE,"E128")}),-1.0]])]});
            var Q70;
            Q70=makeQuery(id+"F0.imprint","IMPRINT",FACE,{"disambiguationData":[TD([[makeQuery(id+"F0.imprint","IMPRINT",EDGE,{"derivedFrom":sQuery(id+"F0.wireOp",EDGE,"E2")}),1.0]])]});
            var Q71;
            Q71=makeQuery(id+"F0.imprint","IMPRINT",FACE,{"disambiguationData":[TD([[makeQuery(id+"F0.imprint","IMPRINT",EDGE,{"derivedFrom":sQuery(id+"F0.wireOp",EDGE,"E6")}),1.0]])]});
            var Q72;
            Q72=makeQuery(id+"F0.imprint","IMPRINT",FACE,{"disambiguationData":[TD([[makeQuery(id+"F0.imprint","IMPRINT",EDGE,{"derivedFrom":sQuery(id+"F0.wireOp",EDGE,"E52")}),-1.0]])]});
            var Q73;
            Q73=makeQuery(id+"F0.imprint","IMPRINT",FACE,{"disambiguationData":[TD([[makeQuery(id+"F0.imprint","IMPRINT",EDGE,{"derivedFrom":sQuery(id+"F0.wireOp",EDGE,"E68")}),-1.0]])]});
            var Q74;
            Q74=makeQuery(id+"F0.imprint","IMPRINT",FACE,{"disambiguationData":[TD([[makeQuery(id+"F0.imprint","IMPRINT",EDGE,{"derivedFrom":sQuery(id+"F0.wireOp",EDGE,"E19")}),1.0]])]});
            var Q75;
            Q75=makeQuery(id+"F0.imprint","IMPRINT",FACE,{"disambiguationData":[TD([[makeQuery(id+"F0.imprint","IMPRINT",EDGE,{"derivedFrom":sQuery(id+"F0.wireOp",EDGE,"E18")}),1.0]])]});
            var Q76;
            Q76=makeQuery(id+"F0.imprint","IMPRINT",FACE,{"disambiguationData":[TD([[makeQuery(id+"F0.imprint","IMPRINT",EDGE,{"derivedFrom":sQuery(id+"F0.wireOp",EDGE,"E90")}),-1.0]])]});
            var Q77;
            Q77=makeQuery(id+"F0.imprint","IMPRINT",FACE,{"disambiguationData":[TD([[makeQuery(id+"F0.imprint","IMPRINT",EDGE,{"derivedFrom":sQuery(id+"F0.wireOp",EDGE,"E7")}),1.0]])]});
            var Q78;
            Q78=makeQuery(id+"F0.imprint","IMPRINT",FACE,{"disambiguationData":[TD([[makeQuery(id+"F0.imprint","IMPRINT",EDGE,{"derivedFrom":sQuery(id+"F0.wireOp",EDGE,"E53")}),-1.0]])]});
            var Q79;
            Q79=makeQuery(id+"F0.imprint","IMPRINT",FACE,{"disambiguationData":[TD([[makeQuery(id+"F0.imprint","IMPRINT",EDGE,{"derivedFrom":sQuery(id+"F0.wireOp",EDGE,"E46")}),1.0]])]});
            var Q80;
            Q80=makeQuery(id+"F0.imprint","IMPRINT",FACE,{"disambiguationData":[TD([[makeQuery(id+"F0.imprint","IMPRINT",EDGE,{"derivedFrom":sQuery(id+"F0.wireOp",EDGE,"E72")}),-1.0]])]});
            var Q81;
            Q81=makeQuery(id+"F0.imprint","IMPRINT",FACE,{"disambiguationData":[TD([[makeQuery(id+"F0.imprint","IMPRINT",EDGE,{"derivedFrom":sQuery(id+"F0.wireOp",EDGE,"E51")}),1.0]])]});
            var Q82;
            Q82=makeQuery(id+"F0.imprint","IMPRINT",FACE,{"disambiguationData":[TD([[makeQuery(id+"F0.imprint","IMPRINT",EDGE,{"derivedFrom":sQuery(id+"F0.wireOp",EDGE,"E73")}),-1.0]])]});
            var Q83;
            Q83=makeQuery(id+"F0.imprint","IMPRINT",FACE,{"disambiguationData":[TD([[makeQuery(id+"F0.imprint","IMPRINT",EDGE,{"derivedFrom":sQuery(id+"F0.wireOp",EDGE,"E21")}),1.0]])]});
            var Q84;
            Q84=makeQuery(id+"F0.imprint","IMPRINT",FACE,{"disambiguationData":[TD([[makeQuery(id+"F0.imprint","IMPRINT",EDGE,{"derivedFrom":sQuery(id+"F0.wireOp",EDGE,"E97")}),-1.0]])]});
            var Q85;
            Q85=makeQuery(id+"F0.imprint","IMPRINT",FACE,{"disambiguationData":[TD([[makeQuery(id+"F0.imprint","IMPRINT",EDGE,{"derivedFrom":sQuery(id+"F0.wireOp",EDGE,"E96")}),1.0]])]});
            var Q86;
            Q86=makeQuery(id+"F0.imprint","IMPRINT",FACE,{"disambiguationData":[TD([[makeQuery(id+"F0.imprint","IMPRINT",EDGE,{"derivedFrom":sQuery(id+"F0.wireOp",EDGE,"E106")}),-1.0]])]});
            var Q87;
            Q87=makeQuery(id+"F0.imprint","IMPRINT",FACE,{"disambiguationData":[TD([[makeQuery(id+"F0.imprint","IMPRINT",EDGE,{"derivedFrom":sQuery(id+"F0.wireOp",EDGE,"E1")}),1.0]])]});
            var Q88;
            Q88=makeQuery(id+"F0.imprint","IMPRINT",FACE,{"disambiguationData":[TD([[makeQuery(id+"F0.imprint","IMPRINT",EDGE,{"derivedFrom":sQuery(id+"F0.wireOp",EDGE,"E32")}),1.0]])]});
            var Q89;
            Q89=makeQuery(id+"F0.imprint","IMPRINT",FACE,{"disambiguationData":[TD([[makeQuery(id+"F0.imprint","IMPRINT",EDGE,{"derivedFrom":sQuery(id+"F0.wireOp",EDGE,"E5")}),1.0]])]});
            var Q90;
            Q90=makeQuery(id+"F0.imprint","IMPRINT",FACE,{"disambiguationData":[TD([[makeQuery(id+"F0.imprint","IMPRINT",EDGE,{"derivedFrom":sQuery(id+"F0.wireOp",EDGE,"E9")}),1.0]])]});
            var Q91;
            Q91=makeQuery(id+"F0.imprint","IMPRINT",FACE,{"disambiguationData":[TD([[makeQuery(id+"F0.imprint","IMPRINT",EDGE,{"derivedFrom":sQuery(id+"F0.wireOp",EDGE,"E25")}),-1.0]])]});
            var Q92;
            Q92=makeQuery(id+"F0.imprint","IMPRINT",FACE,{"disambiguationData":[TD([[makeQuery(id+"F0.imprint","IMPRINT",EDGE,{"derivedFrom":sQuery(id+"F0.wireOp",EDGE,"E16")}),1.0]])]});
            var Q93;
            Q93=makeQuery(id+"F0.imprint","IMPRINT",FACE,{"disambiguationData":[TD([[makeQuery(id+"F0.imprint","IMPRINT",EDGE,{"derivedFrom":sQuery(id+"F0.wireOp",EDGE,"E17")}),-1.0]])]});
            var Q94;
            Q94=makeQuery(id+"F0.imprint","IMPRINT",FACE,{"disambiguationData":[TD([[makeQuery(id+"F0.imprint","IMPRINT",EDGE,{"derivedFrom":sQuery(id+"F0.wireOp",EDGE,"E16")}),-1.0]])]});
            extrude(context, id + "F1", {"entities" : qUnion([Q0, Q1, Q2, Q3, Q4, Q5, Q6, Q7, Q8, Q9, Q10, Q11, Q12, Q13, Q14, Q15, Q16, Q17, Q18, Q19, Q20, Q21, Q22, Q23, Q24, Q25, Q26, Q27, Q28, Q29, Q30, Q31, Q32, Q33, Q34, Q35, Q36, Q37, Q38, Q39, Q40, Q41, Q42, Q43, Q44, Q45, Q46, Q47, Q48, Q49, Q50, Q51, Q52, Q53, Q54, Q55, Q56, Q57, Q58, Q59, Q60, Q61, Q62, Q63, Q64, Q65, Q66, Q67, Q68, Q69, Q70, Q71, Q72, Q73, Q74, Q75, Q76, Q77, Q78, Q79, Q80, Q81, Q82, Q83, Q84, Q85, Q86, Q87, Q88, Q89, Q90, Q91, Q92, Q93, Q94]), "depth" : 3 * mm, "offsetDistance" : 25 * mm});
        }
    });
